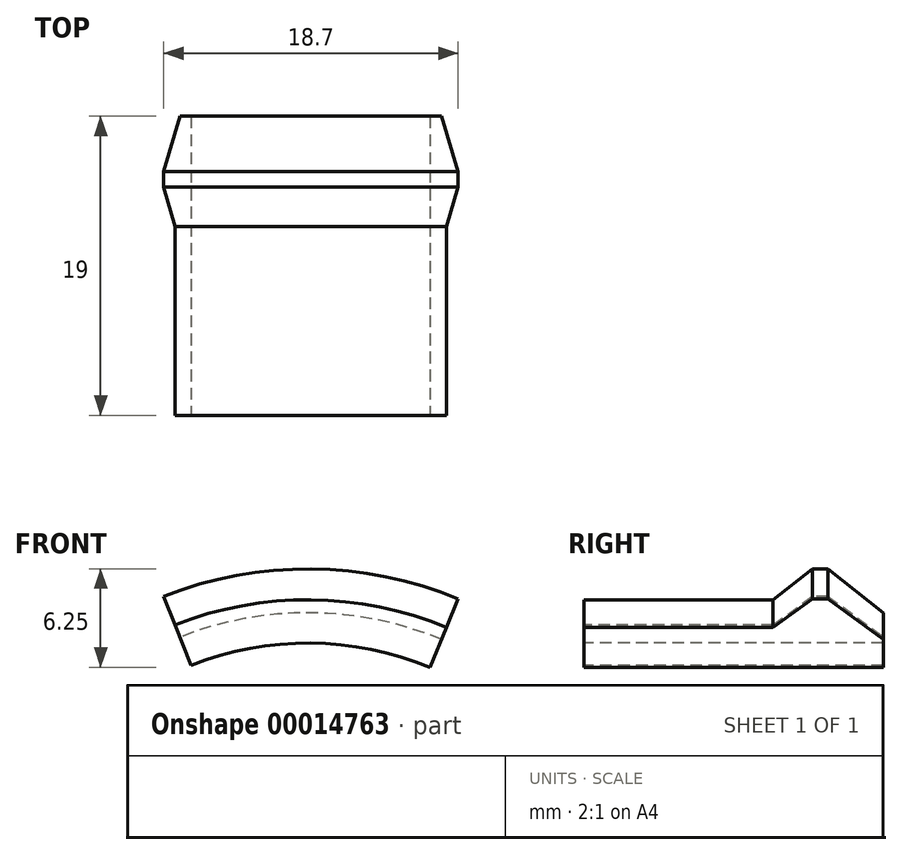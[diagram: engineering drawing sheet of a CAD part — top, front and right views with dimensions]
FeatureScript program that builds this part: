
annotation { "Feature Type Name" : "Feature", "Feature Type Description" : "" }
export const myFeature = defineFeature(function(context is Context, id is Id, definition is map)
    precondition{}
    {
        {
            var Q0;
            Q0=qCreatedBy(makeId("Top.planeOp"),FACE);
            var sketch = newSketch(context, id + "F0", { "sketchPlane" : qUnion([Q0])});
            skLineSegment(sketch, "E0", {"start": v(-7.75, 0) * mm, "end": v(-7.75, 19) * mm});
            skLineSegment(sketch, "E1", {"start": v(-7.75, 19) * mm, "end": v(-5.83, 19) * mm});
            skLineSegment(sketch, "E2", {"start": v(-5.83, 19) * mm, "end": v(-3.04, 15.5) * mm});
            skLineSegment(sketch, "E3", {"start": v(-3.04, 15.5) * mm, "end": v(-3.04, 14.5) * mm});
            skLineSegment(sketch, "E4", {"start": v(-3.04, 14.5) * mm, "end": v(-5, 12) * mm});
            skLineSegment(sketch, "E5", {"start": v(-5, 12) * mm, "end": v(-5, 0) * mm});
            skLineSegment(sketch, "E6", {"start": v(-5, 0) * mm, "end": v(-7.75, 0) * mm});
            skSolve(sketch);
        }
        {
            var Q0;
            Q0=qCreatedBy(makeId("Front.planeOp"),FACE);
            var sketch = newSketch(context, id + "F1", { "sketchPlane" : qUnion([Q0])});
            skCircle(sketch, "E7", {"center": v(-28, 0) * mm, "radius": 23 * mm});
            skSolve(sketch);
        }
        {
            var Q0;
            Q0=makeQuery(id+"F0.imprint","IMPRINT",FACE,{"disambiguationData":[TD([[makeQuery(id+"F0.imprint","IMPRINT",EDGE,{"derivedFrom":sQuery(id+"F0.wireOp",EDGE,"E0")}),-1.0]])]});
            var Q1;
            Q1=sQuery(id+"F1.wireOp",EDGE,"E7");
            sweep(context, id + "F2", {"profiles" : qUnion([Q0]), "path" : qUnion([Q1])});
        }
        {
            var Q0;
            Q0=makeQuery(id+"F2.opSweep","SWEPT_FACE",FACE,{"disambiguationData":[OSD([sQuery(id+"F0.wireOp",EDGE,"E1"),sQuery(id+"F1.wireOp",EDGE,"E7")])]});
            cPlane(context, id + "F3", {"entities" : qUnion([Q0]), "cplaneType" : CPlaneType.OFFSET, "offset" : 0 * mm, "width" : 150 * mm, "height" : 150 * mm});
        }
        {
            var Q0;
            Q0=qCreatedBy(id+"F3.planeOp",FACE);
            var sketch = newSketch(context, id + "F4", { "sketchPlane" : qUnion([Q0])});
            skPoint(sketch, "E8", {"position": v(28, 0) * mm});
            skLineSegment(sketch, "E9", {"start": v(28, 0) * mm, "end": v(37.84, 24.99) * mm});
            skLineSegment(sketch, "E10", {"start": v(28, 0) * mm, "end": v(17.75, 24.74) * mm});
            skLineSegment(sketch, "E11", {"start": v(46.35, 18.96) * mm, "end": v(37.84, 24.99) * mm});
            skLineSegment(sketch, "E12", {"start": v(17.75, 24.74) * mm, "end": v(8.37, 19.63) * mm});
            skArc(sketch, "E13", {"start": v(8.37, 19.63) * mm, "mid": v(26.45, -31.65) * mm, "end": v(46.35, 18.96) * mm});
            skSolve(sketch);
        }
        {
            var Q0;
            Q0=makeQuery(id+"F4.imprint","IMPRINT",FACE,{"disambiguationData":[TD([[makeQuery(id+"F4.imprint","IMPRINT",EDGE,{"derivedFrom":sQuery(id+"F4.wireOp",EDGE,"E9")}),-1.0]])]});
            extrude(context, id + "F5", {"entities" : qUnion([Q0]), "operationType" : NewBodyOperationType.REMOVE, "oppositeDirection" : true, "depth" : 25 * mm});
        }
    });
